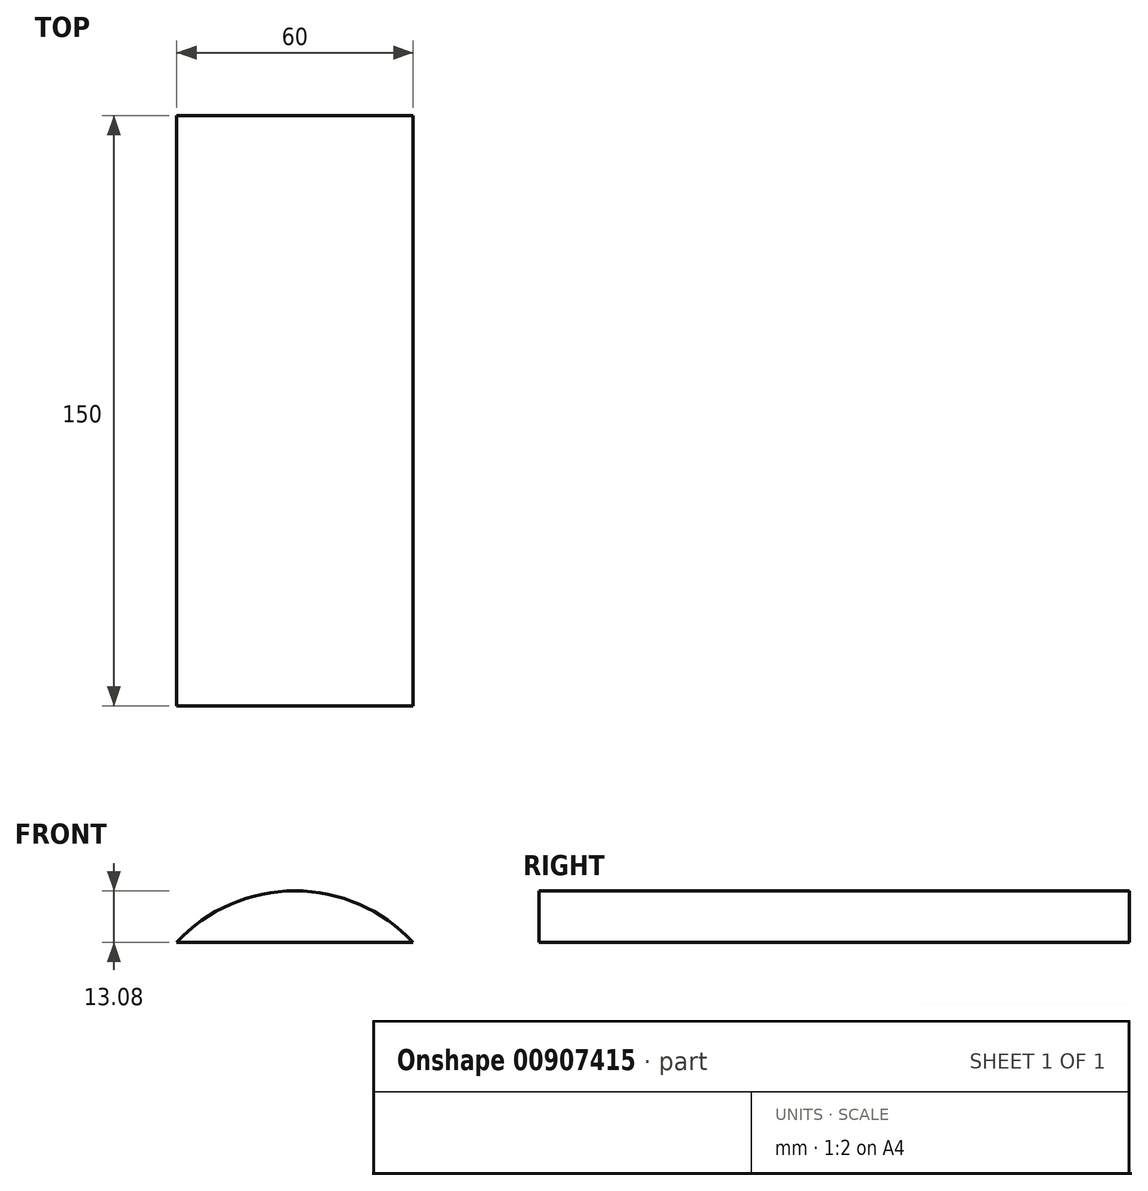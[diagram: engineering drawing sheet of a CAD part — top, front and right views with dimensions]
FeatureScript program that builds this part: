
annotation { "Feature Type Name" : "Feature", "Feature Type Description" : "" }
export const myFeature = defineFeature(function(context is Context, id is Id, definition is map)
    precondition{}
    {
        {
            var Q0;
            Q0=qCreatedBy(makeId("Front.planeOp"),FACE);
            var sketch = newSketch(context, id + "F0", { "sketchPlane" : qUnion([Q0])});
            skLineSegment(sketch, "E0", {"start": v(-21.72, -29.27) * mm, "end": v(38.28, -29.27) * mm});
            skArc(sketch, "E1", {"start": v(38.28, -29.27) * mm, "mid": v(8.28, -16.19) * mm, "end": v(-21.72, -29.27) * mm});
            skSolve(sketch);
        }
        {
            var Q0;
            Q0 = qSketchRegion(id + "F0", true);
            extrude(context, id + "F1", {"entities" : qUnion([Q0]), "depth" : 150 * mm, "offsetDistance" : 25.4 * mm, "symmetric" : true});
        }
    });
